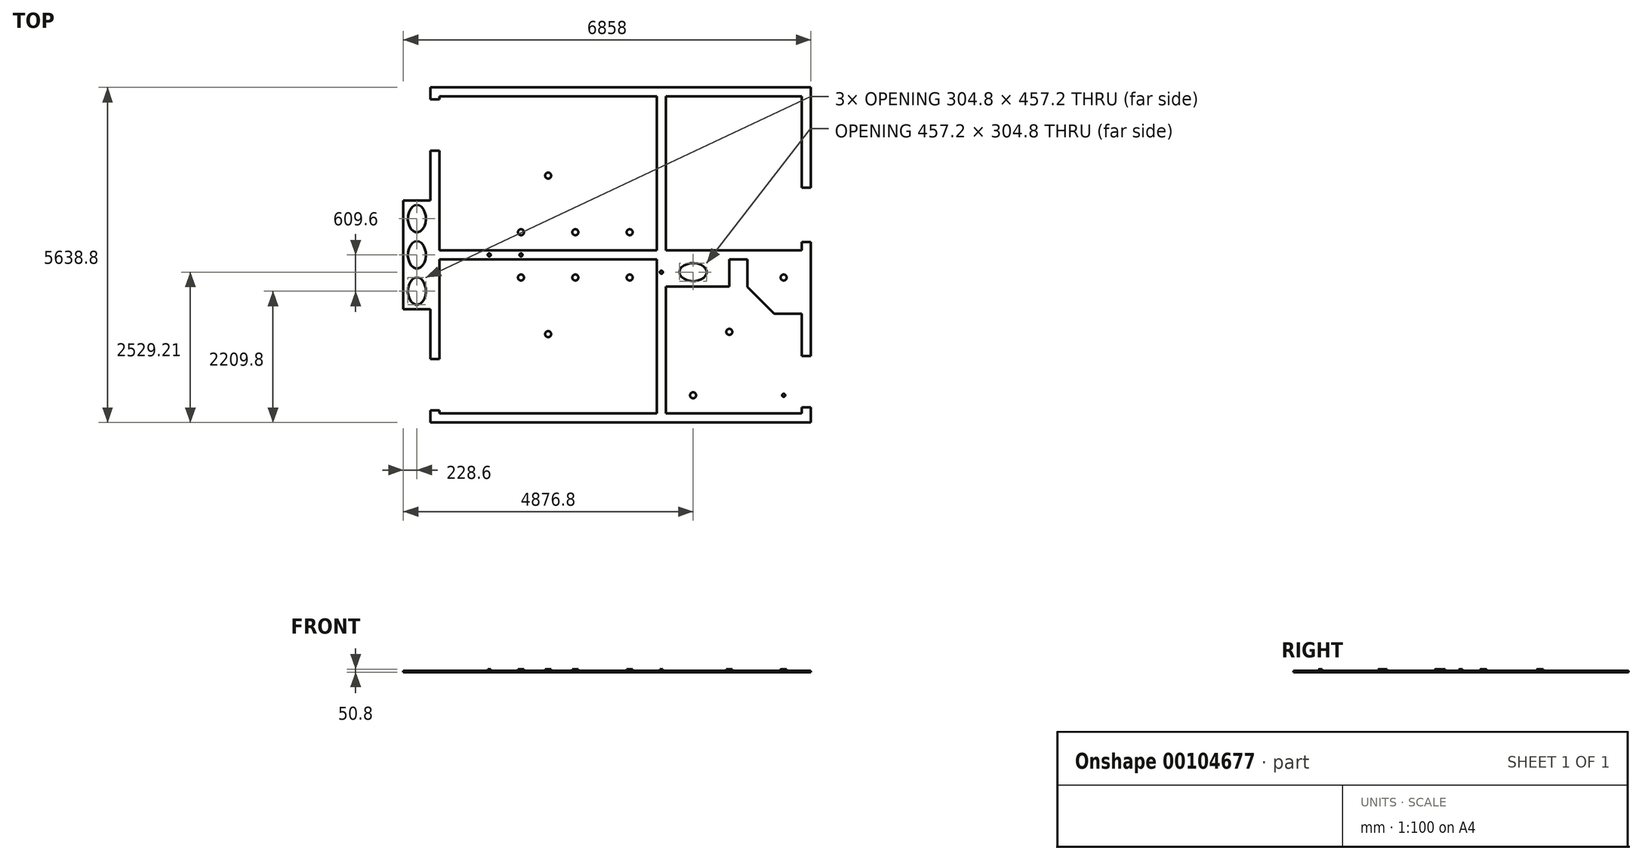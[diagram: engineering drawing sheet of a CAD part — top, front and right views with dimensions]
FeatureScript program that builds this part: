
annotation { "Feature Type Name" : "Feature", "Feature Type Description" : "" }
export const myFeature = defineFeature(function(context is Context, id is Id, definition is map)
    precondition{}
    {
        {
            var Q0;
            Q0=qCreatedBy(makeId("Top.planeOp"),FACE);
            var sketch = newSketch(context, id + "F0", { "sketchPlane" : qUnion([Q0])});
            skLineSegment(sketch, "E0.bottom", {"start": v(0, -6096) * mm, "end": v(7315.2, -6096) * mm, "construction": true});
            skLineSegment(sketch, "E0.left", {"start": v(0, -6096) * mm, "end": v(0, 0) * mm, "construction": true});
            skLineSegment(sketch, "E0.right", {"start": v(7315.2, -6096) * mm, "end": v(7315.2, 0) * mm, "construction": true});
            skLineSegment(sketch, "E1", {"start": v(-8239.1, 0) * mm, "end": v(16647.6, 0) * mm, "construction": true});
            skLineSegment(sketch, "E2", {"start": v(3581.4, 0) * mm, "end": v(3581.4, -228.6) * mm});
            skLineSegment(sketch, "E3", {"start": v(3581.4, -228.6) * mm, "end": v(3733.8, -228.6) * mm});
            skLineSegment(sketch, "E4", {"start": v(3733.8, -228.6) * mm, "end": v(3733.8, 0) * mm});
            skSolve(sketch);
        }
        {
            var Q0;
            Q0=qCreatedBy(makeId("Top.planeOp"),FACE);
            var sketch = newSketch(context, id + "F1", { "sketchPlane" : qUnion([Q0])});
            skLineSegment(sketch, "E5", {"start": v(152.4, -2743.2) * mm, "end": v(3810, -2743.2) * mm});
            skLineSegment(sketch, "E6.MirrorCS", {"start": v(152.4, -2895.6) * mm, "end": v(3810, -2895.6) * mm});
            skLineSegment(sketch, "E7", {"start": v(6400.8, -5638.8) * mm, "end": v(0, -5638.8) * mm});
            skLineSegment(sketch, "E8", {"start": v(0, -4572) * mm, "end": v(0, -1066.8) * mm});
            skLineSegment(sketch, "E9", {"start": v(0, 0) * mm, "end": v(3962.4, 0) * mm});
            skLineSegment(sketch, "E10", {"start": v(3962.4, -152.4) * mm, "end": v(3962.4, -2743.2) * mm});
            skLineSegment(sketch, "E11", {"start": v(3962.4, 0) * mm, "end": v(6400.8, 0) * mm});
            skLineSegment(sketch, "E12", {"start": v(6400.8, 0) * mm, "end": v(6400.8, -1687.1) * mm});
            skLineSegment(sketch, "E13", {"start": v(152.4, -2743.2) * mm, "end": v(152.4, -1066.8) * mm});
            skLineSegment(sketch, "E14", {"start": v(3810, -2743.2) * mm, "end": v(3810, -152.4) * mm});
            skLineSegment(sketch, "E15", {"start": v(3810, -152.4) * mm, "end": v(152.4, -152.4) * mm});
            skLineSegment(sketch, "E16", {"start": v(152.4, -1066.8) * mm, "end": v(0, -1066.8) * mm});
            skLineSegment(sketch, "E17.trimOffspring", {"start": v(0, -203.2) * mm, "end": v(0, 0) * mm});
            skLineSegment(sketch, "E18", {"start": v(0, -5638.8) * mm, "end": v(0, -5435.6) * mm});
            skLineSegment(sketch, "E19", {"start": v(3810, -5486.4) * mm, "end": v(3810, -2895.6) * mm});
            skLineSegment(sketch, "E20", {"start": v(2895.6, -2743.2) * mm, "end": v(2895.6, -1219.2) * mm});
            skLineSegment(sketch, "E21", {"start": v(0, -4572) * mm, "end": v(152.4, -4572) * mm});
            skLineSegment(sketch, "E22", {"start": v(152.4, -4572) * mm, "end": v(152.4, -2895.6) * mm});
            skLineSegment(sketch, "E23", {"start": v(1981.2, -2743.2) * mm, "end": v(1981.2, -1219.2) * mm});
            skLineSegment(sketch, "E24", {"start": v(0, -203.2) * mm, "end": v(152.4, -203.2) * mm});
            skLineSegment(sketch, "E25", {"start": v(152.4, -203.2) * mm, "end": v(152.4, -152.4) * mm});
            skLineSegment(sketch, "E26", {"start": v(0, -5435.6) * mm, "end": v(152.4, -5435.6) * mm});
            skLineSegment(sketch, "E27", {"start": v(152.4, -5435.6) * mm, "end": v(152.4, -5486.4) * mm});
            skLineSegment(sketch, "E28.trimOffspring", {"start": v(152.4, -5486.4) * mm, "end": v(3810, -5486.4) * mm});
            skLineSegment(sketch, "E29", {"start": v(1066.8, -2743.2) * mm, "end": v(1066.8, -1219.2) * mm});
            skLineSegment(sketch, "E30", {"start": v(1066.8, -1219.2) * mm, "end": v(1143, -1219.2) * mm});
            skLineSegment(sketch, "E31", {"start": v(1905, -1219.2) * mm, "end": v(2057.4, -1219.2) * mm});
            skLineSegment(sketch, "E32", {"start": v(2819.4, -1219.2) * mm, "end": v(2971.8, -1219.2) * mm});
            skLineSegment(sketch, "E33", {"start": v(1143, -1219.2) * mm, "end": v(1732.48, -1702.06) * mm});
            skLineSegment(sketch, "E34", {"start": v(3810, -1219.2) * mm, "end": v(3733.8, -1219.2) * mm});
            skLineSegment(sketch, "E35", {"start": v(2057.4, -1219.2) * mm, "end": v(2646.88, -1702.06) * mm});
            skLineSegment(sketch, "E36", {"start": v(2971.8, -1219.2) * mm, "end": v(3561.28, -1702.06) * mm});
            skLineSegment(sketch, "E37", {"start": v(76.2, -203.2) * mm, "end": v(589.55, -897.66) * mm});
            skLineSegment(sketch, "E38", {"start": v(6400.8, -2819.4) * mm, "end": v(0, -2819.4) * mm, "construction": true});
            skLineSegment(sketch, "E39.MirrorCS", {"start": v(76.2, -5435.6) * mm, "end": v(589.55, -4741.14) * mm});
            skLineSegment(sketch, "E40.MirrorCS", {"start": v(1066.8, -4419.6) * mm, "end": v(1143, -4419.6) * mm});
            skLineSegment(sketch, "E41.MirrorCS", {"start": v(2819.4, -4419.6) * mm, "end": v(2971.8, -4419.6) * mm});
            skLineSegment(sketch, "E42.MirrorCS", {"start": v(1905, -4419.6) * mm, "end": v(2057.4, -4419.6) * mm});
            skLineSegment(sketch, "E43.MirrorCS", {"start": v(2971.8, -4419.6) * mm, "end": v(3561.28, -3936.74) * mm});
            skLineSegment(sketch, "E44.MirrorCS", {"start": v(1981.2, -2895.6) * mm, "end": v(1981.2, -4419.6) * mm});
            skLineSegment(sketch, "E45.MirrorCS", {"start": v(1066.8, -2895.6) * mm, "end": v(1066.8, -4419.6) * mm});
            skLineSegment(sketch, "E46.MirrorCS", {"start": v(2057.4, -4419.6) * mm, "end": v(2646.88, -3936.74) * mm});
            skLineSegment(sketch, "E47.MirrorCS", {"start": v(2895.6, -2895.6) * mm, "end": v(2895.6, -4419.6) * mm});
            skLineSegment(sketch, "E48.MirrorCS", {"start": v(3810, -4419.6) * mm, "end": v(3733.8, -4419.6) * mm});
            skLineSegment(sketch, "E49.MirrorCS", {"start": v(1143, -4419.6) * mm, "end": v(1732.48, -3936.74) * mm});
            skLineSegment(sketch, "E50", {"start": v(0, -1905) * mm, "end": v(-457.2, -1905) * mm});
            skLineSegment(sketch, "E51", {"start": v(-457.2, -1905) * mm, "end": v(-457.2, -3733.8) * mm});
            skLineSegment(sketch, "E52", {"start": v(-457.2, -3733.8) * mm, "end": v(0, -3733.8) * mm});
            skEllipse(sketch, "E53", {"center": v(-228.6, -2209.8) * mm, "majorRadius": 228.6 * mm, "minorRadius": 152.4 * mm, "majorAxis": v(0, 1)});
            skEllipse(sketch, "E54", {"center": v(-228.6, -2819.4) * mm, "majorRadius": 228.6 * mm, "minorRadius": 152.4 * mm, "majorAxis": v(0, 1)});
            skEllipse(sketch, "E55", {"center": v(-228.6, -3429) * mm, "majorRadius": 228.6 * mm, "minorRadius": 152.4 * mm, "majorAxis": v(0, 1)});
            skLineSegment(sketch, "E56", {"start": v(3962.4, -2895.6) * mm, "end": v(6248.4, -2895.6) * mm});
            skLineSegment(sketch, "E57", {"start": v(6248.4, -2895.6) * mm, "end": v(6248.4, -4521.2) * mm});
            skLineSegment(sketch, "E58.trimOffspring", {"start": v(3962.4, -2895.6) * mm, "end": v(3962.4, -5486.4) * mm});
            skLineSegment(sketch, "E59.trimOffspring", {"start": v(3962.4, -5486.4) * mm, "end": v(6248.4, -5486.4) * mm});
            skEllipse(sketch, "E60", {"center": v(4419.6, -3109.6) * mm, "majorRadius": 228.6 * mm, "minorRadius": 152.4 * mm, "majorAxis": v(-1, 0)});
            skLineSegment(sketch, "E61", {"start": v(3962.4, -3352.8) * mm, "end": v(5029.2, -3352.8) * mm});
            skLineSegment(sketch, "E62", {"start": v(6248.4, -3810) * mm, "end": v(5784.85, -3810) * mm});
            skLineSegment(sketch, "E63", {"start": v(5334, -3359.15) * mm, "end": v(5784.85, -3810) * mm});
            skLineSegment(sketch, "E64.trimOffspring", {"start": v(5334, -3359.15) * mm, "end": v(5334, -2895.6) * mm});
            skLineSegment(sketch, "E65", {"start": v(3962.4, -152.4) * mm, "end": v(6248.4, -152.4) * mm});
            skLineSegment(sketch, "E66", {"start": v(6248.4, -152.4) * mm, "end": v(6248.4, -1687.1) * mm});
            skLineSegment(sketch, "E67", {"start": v(6248.4, -2743.2) * mm, "end": v(3962.4, -2743.2) * mm});
            skLineSegment(sketch, "E68", {"start": v(6248.4, -2601.5) * mm, "end": v(6400.8, -2601.5) * mm});
            skLineSegment(sketch, "E69", {"start": v(6248.4, -1687.1) * mm, "end": v(6400.8, -1687.1) * mm});
            skLineSegment(sketch, "E70.trimOffspring", {"start": v(6248.4, -2601.5) * mm, "end": v(6248.4, -2743.2) * mm});
            skLineSegment(sketch, "E71.trimOffspring", {"start": v(6400.8, -2601.5) * mm, "end": v(6400.8, -4521.2) * mm});
            skLineSegment(sketch, "E72", {"start": v(5029.2, -3352.8) * mm, "end": v(5029.2, -2895.6) * mm});
            skCircle(sketch, "E73", {"center": v(4419.6, -5181.6) * mm, "radius": 50.8 * mm});
            skLineSegment(sketch, "E74", {"start": v(6248.4, -5384.8) * mm, "end": v(6400.8, -5384.8) * mm});
            skLineSegment(sketch, "E75", {"start": v(6248.4, -4521.2) * mm, "end": v(6400.8, -4521.2) * mm});
            skLineSegment(sketch, "E76.trimOffspring", {"start": v(6400.8, -5384.8) * mm, "end": v(6400.8, -5638.8) * mm});
            skLineSegment(sketch, "E77.trimOffspring", {"start": v(6248.4, -5384.8) * mm, "end": v(6248.4, -5486.4) * mm});
            skLineSegment(sketch, "E78", {"start": v(6324.6, -5384.8) * mm, "end": v(5921.52, -4621.04) * mm});
            skLineSegment(sketch, "E79", {"start": v(6324.6, -2601.5) * mm, "end": v(5876.55, -1804.4) * mm});
            skPoint(sketch, "E80", {"position": v(5105.4, -1447.8) * mm});
            skLineSegment(sketch, "E81", {"start": v(5105.4, -1447.8) * mm, "end": v(4404.46, -2148.74) * mm});
            skLineSegment(sketch, "E82", {"start": v(5105.4, -1447.8) * mm, "end": v(5105.4, -2236.51) * mm, "construction": true});
            skSolve(sketch);
        }
        {
            var Q0;
            Q0=qCreatedBy(makeId("Top.planeOp"),FACE);
            var sketch = newSketch(context, id + "F2", { "sketchPlane" : qUnion([Q0])});
            skCircle(sketch, "E83", {"center": v(1524, -2438.4) * mm, "radius": 50.8 * mm});
            skCircle(sketch, "E84", {"center": v(1524, -3200.4) * mm, "radius": 50.8 * mm});
            skCircle(sketch, "E85", {"center": v(2438.4, -3200.4) * mm, "radius": 50.8 * mm});
            skCircle(sketch, "E86", {"center": v(2438.4, -2438.4) * mm, "radius": 50.8 * mm});
            skCircle(sketch, "E87", {"center": v(3352.8, -2438.4) * mm, "radius": 50.8 * mm});
            skCircle(sketch, "E88", {"center": v(3352.8, -3200.4) * mm, "radius": 50.8 * mm});
            skCircle(sketch, "E89", {"center": v(5943.6, -3200.4) * mm, "radius": 50.8 * mm});
            skCircle(sketch, "E90", {"center": v(3886.2, -3109.6) * mm, "radius": 25.4 * mm});
            skCircle(sketch, "E91", {"center": v(988.97, -2819.4) * mm, "radius": 25.4 * mm});
            skCircle(sketch, "E92", {"center": v(1981.2, -4152.9) * mm, "radius": 50.8 * mm});
            skCircle(sketch, "E93", {"center": v(1981.2, -1485.9) * mm, "radius": 50.8 * mm});
            skCircle(sketch, "E94", {"center": v(5029.2, -4114.8) * mm, "radius": 50.8 * mm});
            skLineSegment(sketch, "E95", {"start": v(1981.2, -1485.9) * mm, "end": v(1981.2, -2794.35) * mm});
            skLineSegment(sketch, "E96", {"start": v(1981.2, -4152.9) * mm, "end": v(1981.2, -2844.46) * mm});
            skLineSegment(sketch, "E97", {"start": v(5029.2, -2667) * mm, "end": v(5029.2, -4165.6) * mm});
            skLineSegment(sketch, "E98", {"start": v(0, -2819.4) * mm, "end": v(1834.75, -2819.4) * mm});
            skLineSegment(sketch, "E99", {"start": v(1524, -2489.2) * mm, "end": v(1524, -2813.12) * mm});
            skLineSegment(sketch, "E100", {"start": v(2438.4, -2489.2) * mm, "end": v(2438.4, -2667) * mm});
            skLineSegment(sketch, "E101", {"start": v(2438.4, -2971.8) * mm, "end": v(2438.4, -3149.6) * mm});
            skLineSegment(sketch, "E102", {"start": v(3352.8, -2489.2) * mm, "end": v(3352.8, -2667) * mm});
            skLineSegment(sketch, "E103", {"start": v(3352.8, -2971.8) * mm, "end": v(3352.8, -3149.6) * mm});
            skLineSegment(sketch, "E104", {"start": v(1979.13, -2819.4) * mm, "end": v(2286, -2819.4) * mm});
            skArc(sketch, "E105.filletArc", {"start": v(2286, -2819.4) * mm, "mid": v(2393.76, -2774.76) * mm, "end": v(2438.4, -2667) * mm});
            skArc(sketch, "E106.filletArc", {"start": v(2438.4, -2971.8) * mm, "mid": v(2393.76, -2864.04) * mm, "end": v(2286, -2819.4) * mm});
            skLineSegment(sketch, "E107", {"start": v(2286, -2819.4) * mm, "end": v(3200.4, -2819.4) * mm});
            skArc(sketch, "E108.filletArc", {"start": v(3200.4, -2819.4) * mm, "mid": v(3308.16, -2774.76) * mm, "end": v(3352.8, -2667) * mm});
            skArc(sketch, "E109.filletArc", {"start": v(3352.8, -2971.8) * mm, "mid": v(3308.16, -2864.04) * mm, "end": v(3200.4, -2819.4) * mm});
            skLineSegment(sketch, "E110", {"start": v(3200.4, -2819.4) * mm, "end": v(3733.8, -2819.4) * mm});
            skLineSegment(sketch, "E111", {"start": v(3733.8, -2819.4) * mm, "end": v(4876.8, -2819.4) * mm});
            skLineSegment(sketch, "E112", {"start": v(4876.8, -2819.4) * mm, "end": v(5638.8, -2819.4) * mm});
            skCircle(sketch, "E113", {"center": v(1524, -2819.4) * mm, "radius": 25.4 * mm});
            skCircle(sketch, "E114", {"center": v(5943.6, -5181.6) * mm, "radius": 25.4 * mm});
            skLineSegment(sketch, "E115", {"start": v(5943.6, -2667) * mm, "end": v(5943.6, -5181.6) * mm});
            skLineSegment(sketch, "E116", {"start": v(4419.6, -3109.6) * mm, "end": v(3886.2, -3109.6) * mm});
            skLineSegment(sketch, "E117", {"start": v(3886.2, -2667) * mm, "end": v(3886.2, -3135) * mm});
            skLineSegment(sketch, "E118", {"start": v(5638.8, -2819.4) * mm, "end": v(5943.6, -2819.4) * mm});
            skSolve(sketch);
        }
        {
            var Q0;
            Q0 = qSketchRegion(id + "F1", true);
            extrude(context, id + "F3", {"entities" : qUnion([Q0]), "depth" : 25.4 * mm, "offsetDistance" : 25.4 * mm});
        }
        {
            var Q0;
            Q0 = qSketchRegion(id + "F2", true);
            extrude(context, id + "F4", {"entities" : qUnion([Q0]), "operationType" : NewBodyOperationType.ADD, "depth" : 50.8 * mm, "offsetDistance" : 25.4 * mm});
        }
    });
